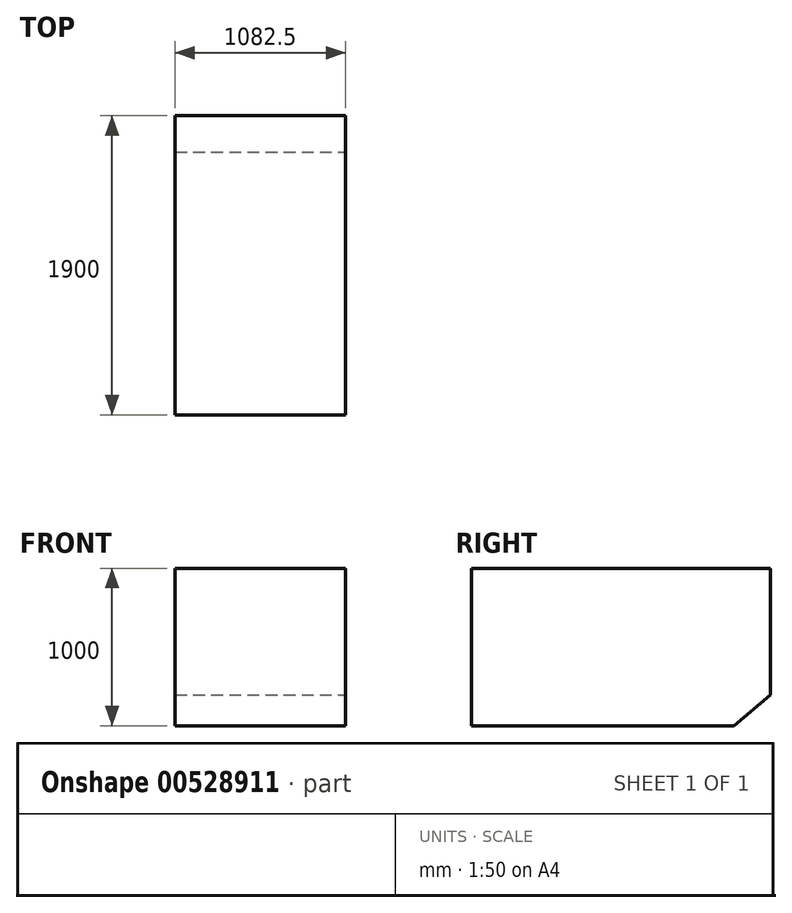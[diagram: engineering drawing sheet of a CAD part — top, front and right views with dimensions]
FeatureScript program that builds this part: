
annotation { "Feature Type Name" : "Feature", "Feature Type Description" : "" }
export const myFeature = defineFeature(function(context is Context, id is Id, definition is map)
    precondition{}
    {
        {
            var Q0;
            Q0=qCreatedBy(makeId("Top.planeOp"),FACE);
            var sketch = newSketch(context, id + "F0", { "sketchPlane" : qUnion([Q0])});
            skLineSegment(sketch, "E0.bottom", {"start": v(0, 0) * mm, "end": v(-1082.5, 0) * mm});
            skLineSegment(sketch, "E0.top", {"start": v(0, 1900) * mm, "end": v(-1082.5, 1900) * mm});
            skLineSegment(sketch, "E0.left", {"start": v(0, 0) * mm, "end": v(0, 1900) * mm});
            skLineSegment(sketch, "E0.right", {"start": v(-1082.5, 0) * mm, "end": v(-1082.5, 1900) * mm});
            skSolve(sketch);
        }
        {
            var Q0;
            Q0=makeQuery(id+"F0.imprint","IMPRINT",FACE,{"disambiguationData":[TD([[makeQuery(id+"F0.imprint","IMPRINT",EDGE,{"derivedFrom":sQuery(id+"F0.wireOp",EDGE,"E0.bottom")}),-1.0]])]});
            extrude(context, id + "F1", {"entities" : qUnion([Q0]), "depth" : 1000 * mm, "offsetDistance" : 25 * mm});
        }
        {
            var Q0;
            Q0=makeQuery(id+"F1.opExtrude","SWEPT_FACE",FACE,{"disambiguationData":[OSD([sQuery(id+"F0.wireOp",EDGE,"E0.left")])]});
            var sketch = newSketch(context, id + "F2", { "sketchPlane" : qUnion([Q0])});
            skLineSegment(sketch, "E1", {"start": v(1900, 0) * mm, "end": v(1900, 500) * mm});
            skLineSegment(sketch, "E2", {"start": v(1900, 194.8) * mm, "end": v(1667.85, 0) * mm});
            skLineSegment(sketch, "E3", {"start": v(1667.85, 0) * mm, "end": v(1900, 0) * mm});
            skCircle(sketch, "E4", {"center": v(1535, 365) * mm, "radius": 365 * mm, "construction": true});
            skLineSegment(sketch, "E5.0", {"start": v(0, 0) * mm, "end": v(1900, 0) * mm, "construction": true});
            skLineSegment(sketch, "E6.0", {"start": v(1900, 1000) * mm, "end": v(1900, 0) * mm, "construction": true});
            skSolve(sketch);
        }
        {
            var Q0;
            {var subQ2=sQuery(id+"F2.wireOp",EDGE,"E2");Q0=makeQuery(id+"F2.imprint","IMPRINT",FACE,{"disambiguationData":[TD([[makeQuery(id+"F2.imprint","IMPRINT",EDGE,{"derivedFrom":subQ2}),1.0]])]});}
            extrude(context, id + "F3", {"entities" : qUnion([Q0]), "operationType" : NewBodyOperationType.REMOVE, "endBound" : BoundingType.THROUGH_ALL, "oppositeDirection" : true, "depth" : 25 * mm, "offsetDistance" : 25 * mm});
        }
    });
